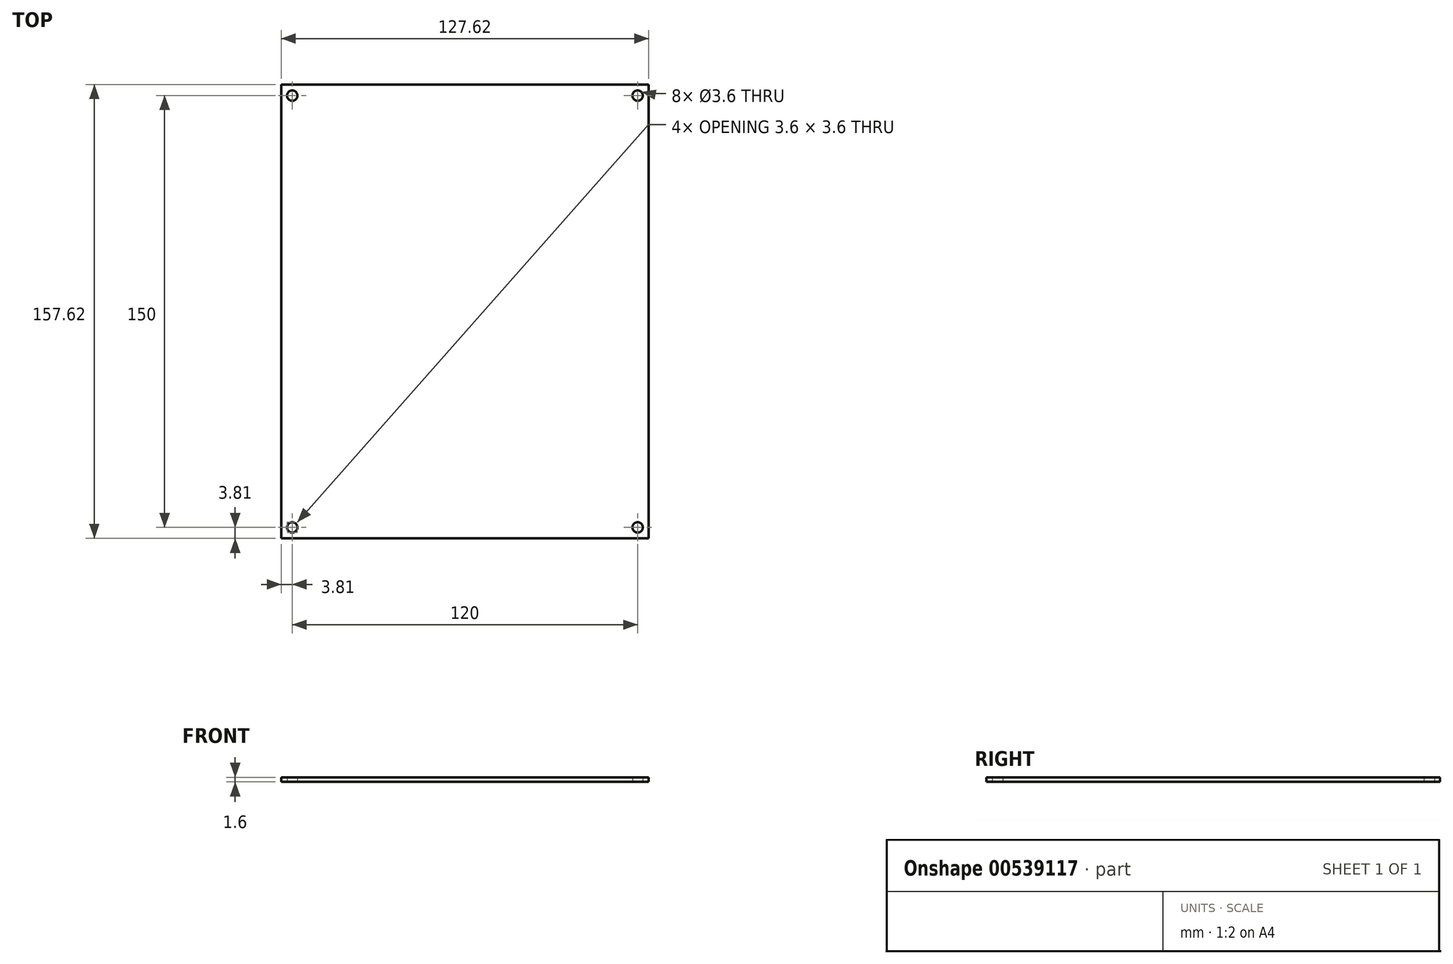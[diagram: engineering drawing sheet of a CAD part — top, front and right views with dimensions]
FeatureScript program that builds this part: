
annotation { "Feature Type Name" : "Feature", "Feature Type Description" : "" }
export const myFeature = defineFeature(function(context is Context, id is Id, definition is map)
    precondition{}
    {
        {
            var Q0;
            Q0=qCreatedBy(makeId("Top.planeOp"),FACE);
            var sketch = newSketch(context, id + "F0", { "sketchPlane" : qUnion([Q0])});
            skLineSegment(sketch, "E0.bottom", {"start": v(0, 0) * mm, "end": v(127.62, 0) * mm});
            skLineSegment(sketch, "E0.top", {"start": v(0, 157.62) * mm, "end": v(127.62, 157.62) * mm});
            skLineSegment(sketch, "E0.left", {"start": v(0, 0) * mm, "end": v(0, 157.62) * mm});
            skLineSegment(sketch, "E0.right", {"start": v(127.62, 0) * mm, "end": v(127.62, 157.62) * mm});
            skLineSegment(sketch, "E1.left", {"start": v(3.8, 153.8) * mm, "end": v(3.81, 3.81) * mm, "construction": true});
            skLineSegment(sketch, "E1.right", {"start": v(123.8, 153.8) * mm, "end": v(123.81, 3.81) * mm, "construction": true});
            skSolve(sketch);
        }
        {
            var Q0;
            Q0=makeQuery(id+"F0.imprint","IMPRINT",FACE,{"disambiguationData":[TD([[makeQuery(id+"F0.imprint","IMPRINT",EDGE,{"derivedFrom":sQuery(id+"F0.wireOp",EDGE,"E0.bottom")}),1.0]])]});
            extrude(context, id + "F1", {"entities" : qUnion([Q0]), "depth" : 1.6 * mm, "offsetDistance" : 25 * mm});
        }
        {
            var Q0;
            Q0=sQuery(id+"F0.wireOp",VERTEX,"E1.left.start");
            var Q1;
            Q1=sQuery(id+"F0.wireOp",VERTEX,"E1.right.start");
            var Q2;
            Q2=sQuery(id+"F0.wireOp",VERTEX,"E1.left.end");
            var Q3;
            Q3=sQuery(id+"F0.wireOp",VERTEX,"E1.right.end");
            var Q4;
            Q4=makeQuery(id+"F1.opExtrude","SWEPT_BODY",BODY,{"disambiguationData":[OSD([sQuery(id+"F0.wireOp",EDGE,"E0.bottom"),sQuery(id+"F0.wireOp",EDGE,"E0.top"),sQuery(id+"F0.wireOp",EDGE,"E0.left"),sQuery(id+"F0.wireOp",EDGE,"E0.right")])]});
            hole(context, id + "F2", {"style" : HoleStyle.SIMPLE, "endStyle" : HoleEndStyle.THROUGH, "oppositeDirection" : true, "holeDiameter" : 3.6 * mm, "isTappedThrough" : true, "tappedDepth" : 12 * mm, "tapClearance" : 3, "locations" : qUnion([Q0, Q1, Q2, Q3]), "scope" : qUnion([Q4])});
        }
    });
